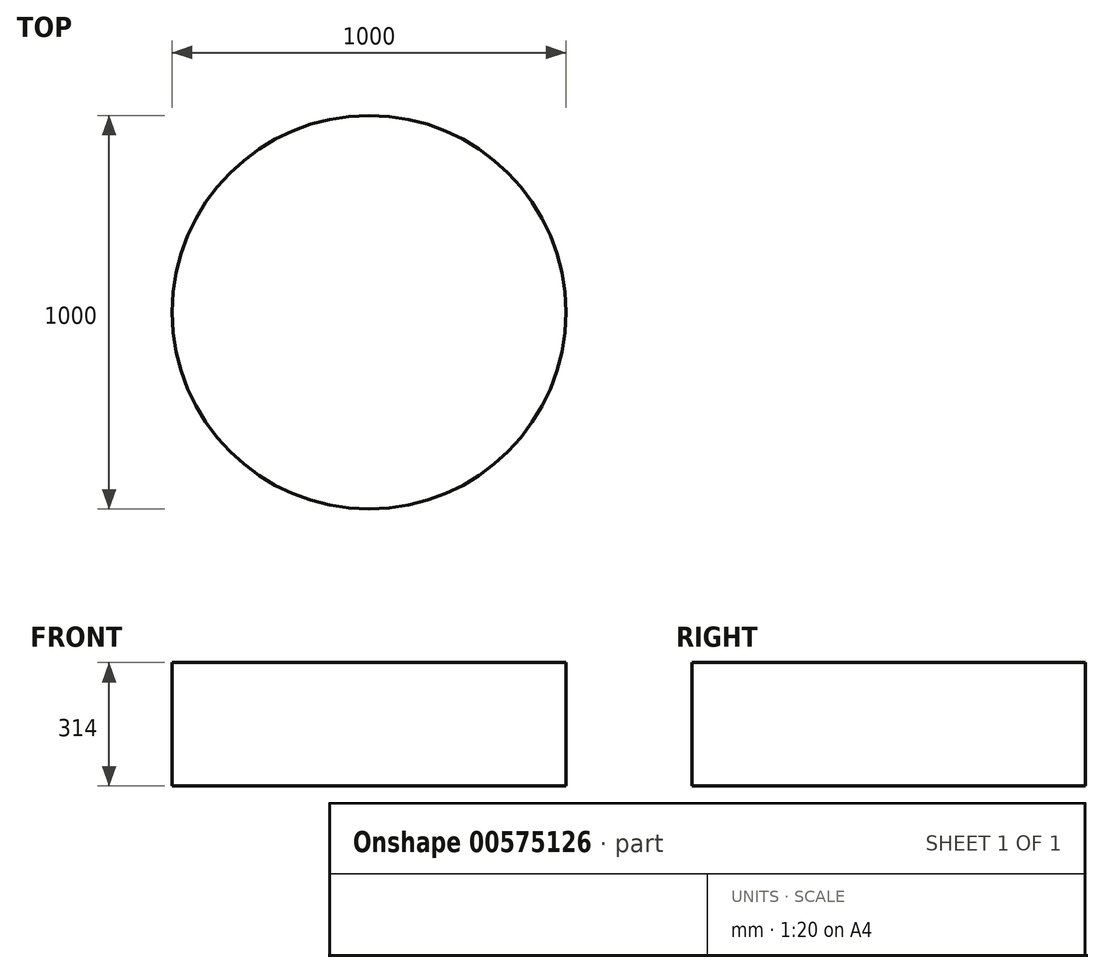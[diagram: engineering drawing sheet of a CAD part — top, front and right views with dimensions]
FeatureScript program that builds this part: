
annotation { "Feature Type Name" : "Feature", "Feature Type Description" : "" }
export const myFeature = defineFeature(function(context is Context, id is Id, definition is map)
    precondition{}
    {
        {
            var Q0;
            Q0=qCreatedBy(makeId("Top.planeOp"),FACE);
            var sketch = newSketch(context, id + "F0", { "sketchPlane" : qUnion([Q0])});
            skCircle(sketch, "E0", {"center": v(0, 0) * mm, "radius": 500 * mm});
            skSolve(sketch);
        }
        {
            var Q0;
            Q0=makeQuery(id+"F0.imprint","IMPRINT",FACE,{"disambiguationData":[TD([[makeQuery(id+"F0.imprint","IMPRINT",EDGE,{"derivedFrom":sQuery(id+"F0.wireOp",EDGE,"E0")}),1.0]])]});
            extrude(context, id + "F1", {"entities" : qUnion([Q0]), "endBound" : BoundingType.SYMMETRIC, "depth" : 314 * mm, "offsetDistance" : 25 * mm});
        }
    });
